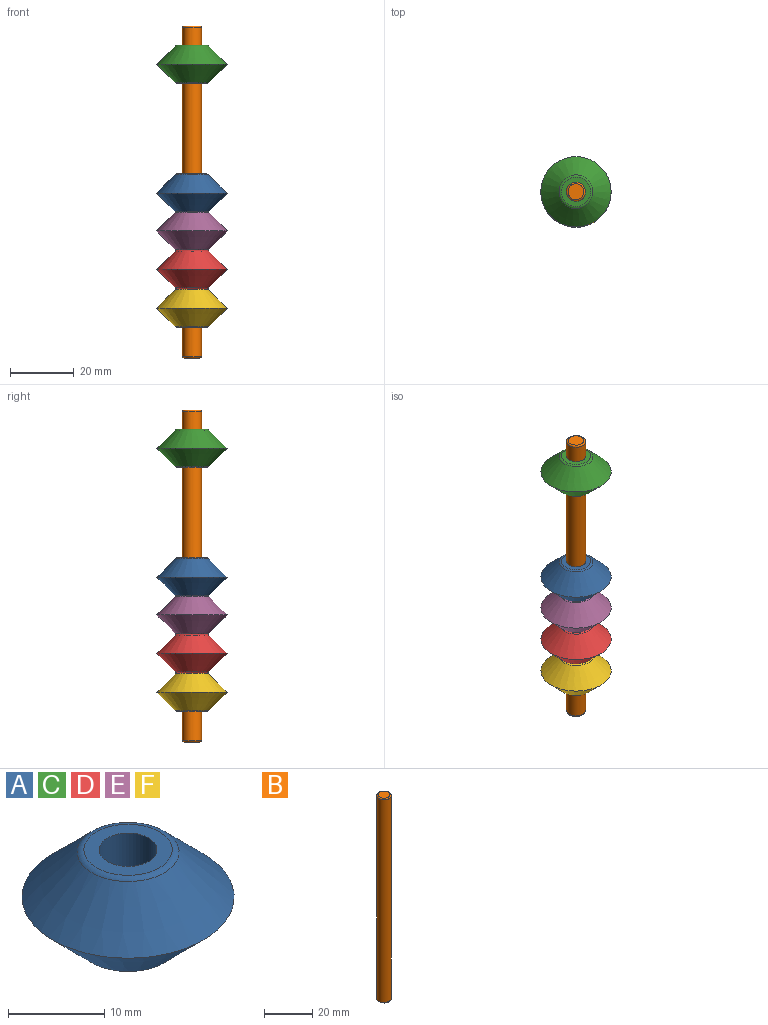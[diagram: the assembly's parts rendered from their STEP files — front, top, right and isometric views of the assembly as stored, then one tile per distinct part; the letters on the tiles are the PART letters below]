
ASSEMBLY  parts=6 mates=5
PART A: 7 faces, bbox 22x22x12 mm
  f0: cylinder r=3mm len=12mm, axis (0,0,1), area 226.2mm2, adj f1,f4
  f1: plane 9.17x9.17mm, normal (0,0,1), area 37.8mm2, adj f0,f5
  f2: cone r=5mm half-angle=45deg, axis (0,0,-1), area 413.1mm2, adj f3,f5
  f3: cone r=11mm half-angle=45deg, axis (0,0,1), area 413.1mm2, adj f2,f6
  f4: plane 9.17x9.17mm, normal (0,0,-1), area 37.8mm2, adj f0,f6
  f5: torus R=4.59mm, axis (0,0,1), area 24.5mm2, adj f1,f2
  f6: torus R=4.59mm, axis (0,0,1), area 24.5mm2, adj f3,f4
PART B: 5 faces, bbox 6.5x6.5x104 mm
  f0: cylinder r=3mm len=103mm, axis (0,0,-1), area 1941.5mm2, adj f3,f4
  f1: plane 5x5mm, normal (0,0,1), area 19.6mm2, adj f4
  f2: plane 5x5mm, normal (0,0,-1), area 19.6mm2, adj f3
  f3: torus R=2.5mm, axis (0,0,1), area 13.9mm2, adj f0,f2
  f4: torus R=2.5mm, axis (0,0,1), area 13.9mm2, adj f0,f1
PART C: same geometry as A
PART D: same geometry as A
PART E: same geometry as A
PART F: same geometry as A
PLACE A rot(axis=(1,0,0),180deg) t=(4.68,11.98,-34.25)mm
PLACE B rot(axis=(1,0,0),180deg) t=(4.68,11.98,-33.92)mm fixed
PLACE C rot(axis=(1,0,0),180deg) t=(4.68,11.98,6.1)mm
PLACE D rot(axis=(1,0,0),180deg) t=(4.68,11.98,-58.17)mm
PLACE E rot(axis=(1,0,0),180deg) t=(4.68,11.98,-46.13)mm
PLACE F t=(4.68,11.98,-70.28)mm
MATE slider A.f0 <-> B.f0  axis (0,0,-1) through (4.68,11.98,-40.25)mm
MATE slider D.f0 <-> B.f0  axis (0,0,-1) through (4.68,11.98,-58.17)mm
MATE slider C.f0 <-> B.f0  axis (0,0,-1) through (4.68,11.98,6.1)mm
MATE slider E.f0 <-> B.f0  axis (0,0,-1) through (4.68,11.98,-46.13)mm
MATE slider F.f0 <-> B.f0  axis (0,0,-1) through (4.68,11.98,-76.28)mm
